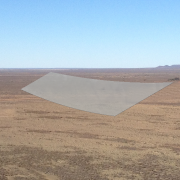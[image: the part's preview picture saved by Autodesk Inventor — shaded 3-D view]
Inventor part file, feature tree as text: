
AUTODESK INVENTOR PART (.ipt)
format: ipt  version: 2013 SP2 (Build 170200200, 200)  size: 150,528 bytes
history: native  units: in
note: dims shown in document units (in); Inventor stores cm internally (conversion verified against a paired STEP export)
features: sketch x3, sweep x1, extrude x1, other x1
ambient origin geometry x8: Origin, YZ Plane, XZ Plane, XY Plane, X Axis, Y Axis, Z Axis, Center Point
feature tree (6):
  sweep  "Sweep2"
  extrude  "Extrusion2"  TaperAngle=0.0deg  [1 undecoded]
  sketch  "Sketch3"  dims[d6=0.0in d7=277.0in d8=60.0in]
  other  "2D Equation Curve2"
  sketch  "Sketch4"  dims[d10=0.25in d11=0.0in]
  sketch  "Sketch7"  dims[d24=78.1in d25=167.1in d26=220.0in d27=1.1853in d28=2.0in d29=2.0in d30=200.0in d31=0.0in]
note: 1 required parameter value undecoded (feature->parameter linkage not recoverable at this tier; creation-order binding heuristic only, values carry confidence <= 0.55)
